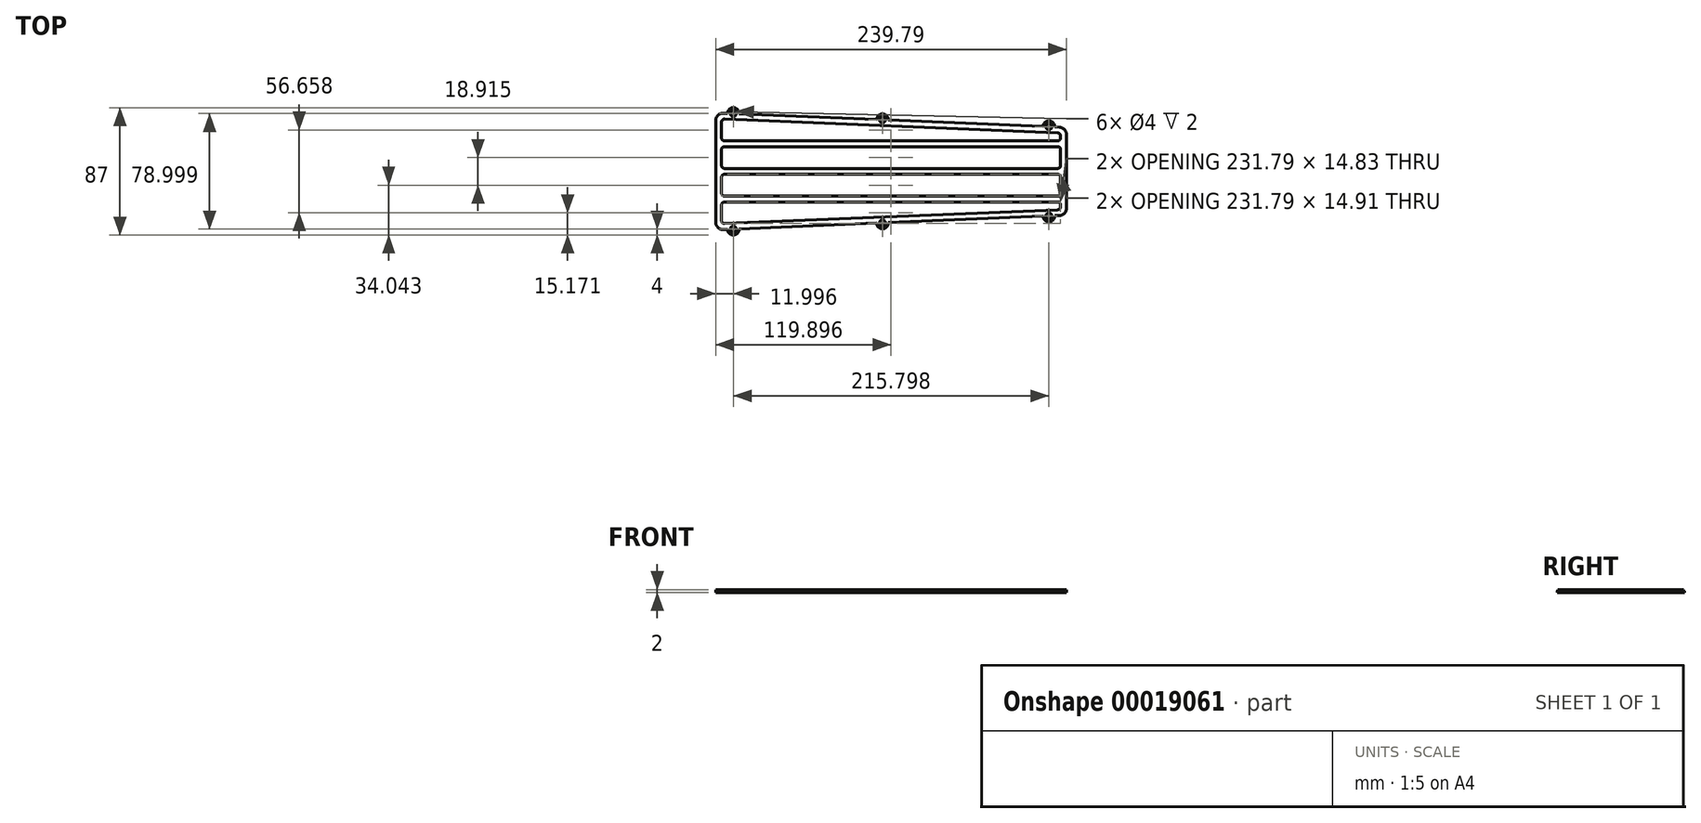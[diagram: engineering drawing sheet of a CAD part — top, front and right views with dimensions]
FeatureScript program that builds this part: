
annotation { "Feature Type Name" : "Feature", "Feature Type Description" : "" }
export const myFeature = defineFeature(function(context is Context, id is Id, definition is map)
    precondition{}
    {
        {
            var Q0;
            Q0=qCreatedBy(makeId("Top.planeOp"),FACE);
            var sketch = newSketch(context, id + "F0", { "sketchPlane" : qUnion([Q0])});
            skLineSegment(sketch, "E0.top", {"start": v(0, 80) * mm, "end": v(239.8, 70) * mm});
            skLineSegment(sketch, "E0.left", {"start": v(0, 0) * mm, "end": v(0, 80) * mm});
            skLineSegment(sketch, "E0.right", {"start": v(239.8, 10) * mm, "end": v(239.8, 70) * mm});
            skLineSegment(sketch, "E1", {"start": v(0, 0) * mm, "end": v(239.8, 10) * mm});
            skLineSegment(sketch, "E2", {"start": v(0, 40) * mm, "end": v(239.8, 40) * mm, "construction": true});
            skSolve(sketch);
        }
        {
            var Q0;
            Q0 = qSketchRegion(id + "F0", true);
            extrude(context, id + "F1", {"entities" : qUnion([Q0]), "depth" : 2 * mm});
        }
        {
            var Q0;
            Q0=makeQuery(id+"F1.opExtrude","CAP_FACE",FACE,{"disambiguationData":[OSD([sQuery(id+"F0.wireOp",EDGE,"E0.top"),sQuery(id+"F0.wireOp",EDGE,"E0.left"),sQuery(id+"F0.wireOp",EDGE,"E0.right"),sQuery(id+"F0.wireOp",EDGE,"E1")])],"isStart":false});
            var sketch = newSketch(context, id + "F2", { "sketchPlane" : qUnion([Q0])});
            skLineSegment(sketch, "E3", {"start": v(4, 75.83) * mm, "end": v(4, 60.91) * mm});
            skLineSegment(sketch, "E4", {"start": v(4, 60.91) * mm, "end": v(235.8, 60.91) * mm});
            skLineSegment(sketch, "E5", {"start": v(235.8, 60.91) * mm, "end": v(235.8, 66.16) * mm});
            skLineSegment(sketch, "E6", {"start": v(235.8, 66.16) * mm, "end": v(4, 75.83) * mm});
            skLineSegment(sketch, "E7", {"start": v(4, 19.09) * mm, "end": v(4, 4.17) * mm});
            skLineSegment(sketch, "E8", {"start": v(4, 4.17) * mm, "end": v(235.8, 13.84) * mm});
            skLineSegment(sketch, "E9", {"start": v(235.8, 13.84) * mm, "end": v(235.8, 19.09) * mm});
            skLineSegment(sketch, "E10", {"start": v(235.8, 19.09) * mm, "end": v(4, 19.09) * mm});
            skLineSegment(sketch, "E11", {"start": v(4, 23.09) * mm, "end": v(4, 38) * mm});
            skLineSegment(sketch, "E12", {"start": v(4, 23.09) * mm, "end": v(235.8, 23.09) * mm});
            skLineSegment(sketch, "E13", {"start": v(235.8, 38) * mm, "end": v(235.8, 23.09) * mm});
            skLineSegment(sketch, "E14", {"start": v(235.8, 38) * mm, "end": v(4, 38) * mm});
            skLineSegment(sketch, "E15", {"start": v(4, 42) * mm, "end": v(4, 56.91) * mm});
            skLineSegment(sketch, "E16", {"start": v(4, 42) * mm, "end": v(235.8, 42) * mm});
            skLineSegment(sketch, "E17", {"start": v(235.8, 56.91) * mm, "end": v(235.8, 42) * mm});
            skLineSegment(sketch, "E18", {"start": v(235.8, 56.91) * mm, "end": v(4, 56.91) * mm});
            skLineSegment(sketch, "E19", {"start": v(235.8, 60.91) * mm, "end": v(235.8, 56.91) * mm, "construction": true});
            skLineSegment(sketch, "E20", {"start": v(235.8, 42) * mm, "end": v(235.8, 38) * mm, "construction": true});
            skLineSegment(sketch, "E21", {"start": v(235.8, 23.09) * mm, "end": v(235.8, 19.09) * mm, "construction": true});
            skLineSegment(sketch, "E22", {"start": v(0, 40) * mm, "end": v(235.8, 40) * mm, "construction": true});
            skSolve(sketch);
        }
        {
            var Q0;
            Q0 = qSketchRegion(id + "F2", true);
            extrude(context, id + "F3", {"entities" : qUnion([Q0]), "operationType" : NewBodyOperationType.REMOVE, "oppositeDirection" : true, "depth" : 25 * mm});
        }
        {
            var Q0;
            Q0=makeQuery(id+"F3.boolean.opBoolean","COPY",EDGE,{"derivedFrom":makeQuery(id+"F3.opExtrude","SWEPT_EDGE",EDGE,{"disambiguationData":[OSD([sQuery(id+"F2.wireOp",EDGE,"E3"),sQuery(id+"F2.wireOp",EDGE,"E6")])]})});
            var Q1;
            Q1=makeQuery(id+"F3.boolean.opBoolean","COPY",EDGE,{"derivedFrom":makeQuery(id+"F3.opExtrude","SWEPT_EDGE",EDGE,{"disambiguationData":[OSD([sQuery(id+"F2.wireOp",EDGE,"E3"),sQuery(id+"F2.wireOp",EDGE,"E4")])]})});
            var Q2;
            Q2=makeQuery(id+"F3.boolean.opBoolean","COPY",EDGE,{"derivedFrom":makeQuery(id+"F3.opExtrude","SWEPT_EDGE",EDGE,{"disambiguationData":[OSD([sQuery(id+"F2.wireOp",EDGE,"E15"),sQuery(id+"F2.wireOp",EDGE,"E18")])]})});
            var Q3;
            Q3=makeQuery(id+"F3.boolean.opBoolean","COPY",EDGE,{"derivedFrom":makeQuery(id+"F3.opExtrude","SWEPT_EDGE",EDGE,{"disambiguationData":[OSD([sQuery(id+"F2.wireOp",EDGE,"E15"),sQuery(id+"F2.wireOp",EDGE,"E16")])]})});
            var Q4;
            Q4=makeQuery(id+"F3.boolean.opBoolean","COPY",EDGE,{"derivedFrom":makeQuery(id+"F3.opExtrude","SWEPT_EDGE",EDGE,{"disambiguationData":[OSD([sQuery(id+"F2.wireOp",EDGE,"E11"),sQuery(id+"F2.wireOp",EDGE,"E14")])]})});
            var Q5;
            Q5=makeQuery(id+"F3.boolean.opBoolean","COPY",EDGE,{"derivedFrom":makeQuery(id+"F3.opExtrude","SWEPT_EDGE",EDGE,{"disambiguationData":[OSD([sQuery(id+"F2.wireOp",EDGE,"E11"),sQuery(id+"F2.wireOp",EDGE,"E12")])]})});
            var Q6;
            Q6=makeQuery(id+"F3.boolean.opBoolean","COPY",EDGE,{"derivedFrom":makeQuery(id+"F3.opExtrude","SWEPT_EDGE",EDGE,{"disambiguationData":[OSD([sQuery(id+"F2.wireOp",EDGE,"E7"),sQuery(id+"F2.wireOp",EDGE,"E8")])]})});
            var Q7;
            Q7=makeQuery(id+"F3.boolean.opBoolean","COPY",EDGE,{"derivedFrom":makeQuery(id+"F3.opExtrude","SWEPT_EDGE",EDGE,{"disambiguationData":[OSD([sQuery(id+"F2.wireOp",EDGE,"E7"),sQuery(id+"F2.wireOp",EDGE,"E10")])]})});
            var Q8;
            Q8=makeQuery(id+"F3.boolean.opBoolean","COPY",EDGE,{"derivedFrom":makeQuery(id+"F3.opExtrude","SWEPT_EDGE",EDGE,{"disambiguationData":[OSD([sQuery(id+"F2.wireOp",EDGE,"E5"),sQuery(id+"F2.wireOp",EDGE,"E6")])]})});
            var Q9;
            Q9=makeQuery(id+"F3.boolean.opBoolean","COPY",EDGE,{"derivedFrom":makeQuery(id+"F3.opExtrude","SWEPT_EDGE",EDGE,{"disambiguationData":[OSD([sQuery(id+"F2.wireOp",EDGE,"E4"),sQuery(id+"F2.wireOp",EDGE,"E5")])]})});
            var Q10;
            Q10=makeQuery(id+"F3.boolean.opBoolean","COPY",EDGE,{"derivedFrom":makeQuery(id+"F3.opExtrude","SWEPT_EDGE",EDGE,{"disambiguationData":[OSD([sQuery(id+"F2.wireOp",EDGE,"E16"),sQuery(id+"F2.wireOp",EDGE,"E17")])]})});
            var Q11;
            Q11=makeQuery(id+"F3.boolean.opBoolean","COPY",EDGE,{"derivedFrom":makeQuery(id+"F3.opExtrude","SWEPT_EDGE",EDGE,{"disambiguationData":[OSD([sQuery(id+"F2.wireOp",EDGE,"E17"),sQuery(id+"F2.wireOp",EDGE,"E18")])]})});
            var Q12;
            Q12=makeQuery(id+"F3.boolean.opBoolean","COPY",EDGE,{"derivedFrom":makeQuery(id+"F3.opExtrude","SWEPT_EDGE",EDGE,{"disambiguationData":[OSD([sQuery(id+"F2.wireOp",EDGE,"E13"),sQuery(id+"F2.wireOp",EDGE,"E14")])]})});
            var Q13;
            Q13=makeQuery(id+"F3.boolean.opBoolean","COPY",EDGE,{"derivedFrom":makeQuery(id+"F3.opExtrude","SWEPT_EDGE",EDGE,{"disambiguationData":[OSD([sQuery(id+"F2.wireOp",EDGE,"E12"),sQuery(id+"F2.wireOp",EDGE,"E13")])]})});
            var Q14;
            Q14=makeQuery(id+"F3.boolean.opBoolean","COPY",EDGE,{"derivedFrom":makeQuery(id+"F3.opExtrude","SWEPT_EDGE",EDGE,{"disambiguationData":[OSD([sQuery(id+"F2.wireOp",EDGE,"E8"),sQuery(id+"F2.wireOp",EDGE,"E9")])]})});
            var Q15;
            Q15=makeQuery(id+"F3.boolean.opBoolean","COPY",EDGE,{"derivedFrom":makeQuery(id+"F3.opExtrude","SWEPT_EDGE",EDGE,{"disambiguationData":[OSD([sQuery(id+"F2.wireOp",EDGE,"E9"),sQuery(id+"F2.wireOp",EDGE,"E10")])]})});
            fillet(context, id + "F4", {"entities" : qUnion([Q0, Q1, Q2, Q3, Q4, Q5, Q6, Q7, Q8, Q9, Q10, Q11, Q12, Q13, Q14, Q15]), "radius" : 2 * mm, "tangentPropagation" : true, "allowEdgeOverflow" : false});
        }
        {
            var Q0;
            Q0=makeQuery(id+"F1.opExtrude","SWEPT_EDGE",EDGE,{"disambiguationData":[OSD([sQuery(id+"F0.wireOp",EDGE,"E0.right"),sQuery(id+"F0.wireOp",EDGE,"E1")])]});
            var Q1;
            Q1=makeQuery(id+"F1.opExtrude","SWEPT_EDGE",EDGE,{"disambiguationData":[OSD([sQuery(id+"F0.wireOp",EDGE,"E0.top"),sQuery(id+"F0.wireOp",EDGE,"E0.right")])]});
            var Q2;
            Q2=makeQuery(id+"F1.opExtrude","SWEPT_EDGE",EDGE,{"disambiguationData":[OSD([sQuery(id+"F0.wireOp",EDGE,"E0.left"),sQuery(id+"F0.wireOp",EDGE,"E1")])]});
            var Q3;
            Q3=makeQuery(id+"F1.opExtrude","SWEPT_EDGE",EDGE,{"disambiguationData":[OSD([sQuery(id+"F0.wireOp",EDGE,"E0.top"),sQuery(id+"F0.wireOp",EDGE,"E0.left")])]});
            fillet(context, id + "F5", {"entities" : qUnion([Q0, Q1, Q2, Q3]), "radius" : 5 * mm, "tangentPropagation" : true, "allowEdgeOverflow" : false});
        }
        {
            var Q0;
            Q0=makeQuery(id+"F1.opExtrude","CAP_FACE",FACE,{"disambiguationData":[OSD([sQuery(id+"F0.wireOp",EDGE,"E0.top"),sQuery(id+"F0.wireOp",EDGE,"E0.left"),sQuery(id+"F0.wireOp",EDGE,"E0.right"),sQuery(id+"F0.wireOp",EDGE,"E1")])],"isStart":false});
            var sketch = newSketch(context, id + "F6", { "sketchPlane" : qUnion([Q0])});
            skArc(sketch, "E23", {"start": v(16, 79.33) * mm, "mid": v(12.16, 83.5) * mm, "end": v(8, 79.67) * mm});
            skLineSegment(sketch, "E24", {"start": v(8, 79.67) * mm, "end": v(16, 79.33) * mm});
            skLineSegment(sketch, "E25", {"start": v(8, 79.67) * mm, "end": v(8, 0.33) * mm, "construction": true});
            skArc(sketch, "E26", {"start": v(8, 0.33) * mm, "mid": v(12.16, -3.5) * mm, "end": v(16, 0.67) * mm});
            skLineSegment(sketch, "E27", {"start": v(8, 0.33) * mm, "end": v(16, 0.67) * mm});
            skLineSegment(sketch, "E28", {"start": v(231.8, 70.33) * mm, "end": v(231.8, 9.67) * mm, "construction": true});
            skArc(sketch, "E29", {"start": v(231.8, 70.33) * mm, "mid": v(227.96, 74.5) * mm, "end": v(223.8, 70.67) * mm});
            skArc(sketch, "E30", {"start": v(223.8, 9.33) * mm, "mid": v(227.96, 5.5) * mm, "end": v(231.8, 9.67) * mm});
            skLineSegment(sketch, "E31", {"start": v(223.8, 70.67) * mm, "end": v(231.8, 70.33) * mm});
            skLineSegment(sketch, "E32", {"start": v(231.8, 9.67) * mm, "end": v(223.8, 9.33) * mm});
            skLineSegment(sketch, "E33", {"start": v(110, 75.41) * mm, "end": v(110, 4.59) * mm, "construction": true});
            skArc(sketch, "E34", {"start": v(118, 75.08) * mm, "mid": v(114.16, 79.24) * mm, "end": v(110, 75.41) * mm});
            skArc(sketch, "E35", {"start": v(110, 4.59) * mm, "mid": v(114.16, 0.76) * mm, "end": v(118, 4.92) * mm});
            skLineSegment(sketch, "E36", {"start": v(110, 75.41) * mm, "end": v(118, 75.08) * mm});
            skLineSegment(sketch, "E37", {"start": v(110, 4.59) * mm, "end": v(118, 4.92) * mm});
            skSolve(sketch);
        }
        {
            var Q0;
            Q0 = qSketchRegion(id + "F6", true);
            var Q1;
            Q1=makeQuery(id+"F1.opExtrude","CAP_FACE",FACE,{"disambiguationData":[OSD([sQuery(id+"F0.wireOp",EDGE,"E0.top"),sQuery(id+"F0.wireOp",EDGE,"E0.left"),sQuery(id+"F0.wireOp",EDGE,"E0.right"),sQuery(id+"F0.wireOp",EDGE,"E1")])],"isStart":true});
            extrude(context, id + "F7", {"entities" : qUnion([Q0]), "operationType" : NewBodyOperationType.ADD, "endBound" : BoundingType.UP_TO_SURFACE, "oppositeDirection" : true, "endBoundEntityFace" : qUnion([Q1]), "depth" : 25 * mm});
        }
        {
            var Q0;
            Q0=makeQuery(id+"F7.boolean.opBoolean","MERGE",FACE,{"derivedFrom":[makeQuery(id+"F1.opExtrude","CAP_FACE",FACE,{"disambiguationData":[OSD([sQuery(id+"F0.wireOp",EDGE,"E0.top"),sQuery(id+"F0.wireOp",EDGE,"E0.left"),sQuery(id+"F0.wireOp",EDGE,"E0.right"),sQuery(id+"F0.wireOp",EDGE,"E1")])],"isStart":false}),makeQuery(id+"F7.opExtrude","CAP_FACE",FACE,{"disambiguationData":[OSD([sQuery(id+"F6.wireOp",EDGE,"E23"),sQuery(id+"F6.wireOp",EDGE,"E24")])],"isStart":true}),makeQuery(id+"F7.opExtrude","CAP_FACE",FACE,{"disambiguationData":[OSD([sQuery(id+"F6.wireOp",EDGE,"E26"),sQuery(id+"F6.wireOp",EDGE,"E27")])],"isStart":true}),makeQuery(id+"F7.opExtrude","CAP_FACE",FACE,{"disambiguationData":[OSD([sQuery(id+"F6.wireOp",EDGE,"E29"),sQuery(id+"F6.wireOp",EDGE,"E31")])],"isStart":true}),makeQuery(id+"F7.opExtrude","CAP_FACE",FACE,{"disambiguationData":[OSD([sQuery(id+"F6.wireOp",EDGE,"E30"),sQuery(id+"F6.wireOp",EDGE,"E32")])],"isStart":true}),makeQuery(id+"F7.opExtrude","CAP_FACE",FACE,{"disambiguationData":[OSD([sQuery(id+"F6.wireOp",EDGE,"E34"),sQuery(id+"F6.wireOp",EDGE,"E36")])],"isStart":true}),makeQuery(id+"F7.opExtrude","CAP_FACE",FACE,{"disambiguationData":[OSD([sQuery(id+"F6.wireOp",EDGE,"E35"),sQuery(id+"F6.wireOp",EDGE,"E37")])],"isStart":true})]});
            var sketch = newSketch(context, id + "F8", { "sketchPlane" : qUnion([Q0])});
            skCircle(sketch, "E38", {"center": v(12, 79.5) * mm, "radius": 2 * mm});
            skCircle(sketch, "E39", {"center": v(114, 75.25) * mm, "radius": 2 * mm});
            skCircle(sketch, "E40", {"center": v(227.8, 70.5) * mm, "radius": 2 * mm});
            skCircle(sketch, "E41", {"center": v(227.8, 9.5) * mm, "radius": 2 * mm});
            skCircle(sketch, "E42", {"center": v(114, 4.75) * mm, "radius": 2 * mm});
            skCircle(sketch, "E43", {"center": v(12, 0.5) * mm, "radius": 2 * mm});
            skSolve(sketch);
        }
        {
            var Q0;
            Q0 = qSketchRegion(id + "F8", true);
            extrude(context, id + "F9", {"entities" : qUnion([Q0]), "operationType" : NewBodyOperationType.REMOVE, "oppositeDirection" : true, "depth" : 25 * mm});
        }
        {
            var Q0;
            Q0=makeQuery(id+"F7.boolean.opBoolean","MERGE",FACE,{"derivedFrom":[makeQuery(id+"F1.opExtrude","CAP_FACE",FACE,{"disambiguationData":[OSD([sQuery(id+"F0.wireOp",EDGE,"E0.top"),sQuery(id+"F0.wireOp",EDGE,"E0.left"),sQuery(id+"F0.wireOp",EDGE,"E0.right"),sQuery(id+"F0.wireOp",EDGE,"E1")])],"isStart":false}),makeQuery(id+"F7.opExtrude","CAP_FACE",FACE,{"disambiguationData":[OSD([sQuery(id+"F6.wireOp",EDGE,"E23"),sQuery(id+"F6.wireOp",EDGE,"E24")])],"isStart":true}),makeQuery(id+"F7.opExtrude","CAP_FACE",FACE,{"disambiguationData":[OSD([sQuery(id+"F6.wireOp",EDGE,"E26"),sQuery(id+"F6.wireOp",EDGE,"E27")])],"isStart":true}),makeQuery(id+"F7.opExtrude","CAP_FACE",FACE,{"disambiguationData":[OSD([sQuery(id+"F6.wireOp",EDGE,"E29"),sQuery(id+"F6.wireOp",EDGE,"E31")])],"isStart":true}),makeQuery(id+"F7.opExtrude","CAP_FACE",FACE,{"disambiguationData":[OSD([sQuery(id+"F6.wireOp",EDGE,"E30"),sQuery(id+"F6.wireOp",EDGE,"E32")])],"isStart":true}),makeQuery(id+"F7.opExtrude","CAP_FACE",FACE,{"disambiguationData":[OSD([sQuery(id+"F6.wireOp",EDGE,"E34"),sQuery(id+"F6.wireOp",EDGE,"E36")])],"isStart":true}),makeQuery(id+"F7.opExtrude","CAP_FACE",FACE,{"disambiguationData":[OSD([sQuery(id+"F6.wireOp",EDGE,"E35"),sQuery(id+"F6.wireOp",EDGE,"E37")])],"isStart":true})]});
            var sketch = newSketch(context, id + "F10", { "sketchPlane" : qUnion([Q0])});
            skLineSegment(sketch, "E44.bottom", {"start": v(10, 83.5) * mm, "end": v(14, 83.5) * mm});
            skLineSegment(sketch, "E44.top", {"start": v(10, 79.5) * mm, "end": v(14, 79.5) * mm});
            skLineSegment(sketch, "E44.left", {"start": v(10, 83.5) * mm, "end": v(10, 79.5) * mm});
            skLineSegment(sketch, "E44.right", {"start": v(14, 83.5) * mm, "end": v(14, 79.5) * mm});
            skLineSegment(sketch, "E45.bottom", {"start": v(112, 79.25) * mm, "end": v(116, 79.25) * mm});
            skLineSegment(sketch, "E45.top", {"start": v(112, 75.25) * mm, "end": v(116, 75.25) * mm});
            skLineSegment(sketch, "E45.left", {"start": v(112, 79.25) * mm, "end": v(112, 75.25) * mm});
            skLineSegment(sketch, "E45.right", {"start": v(116, 79.25) * mm, "end": v(116, 75.25) * mm});
            skLineSegment(sketch, "E46.bottom", {"start": v(225.8, 74.5) * mm, "end": v(229.8, 74.5) * mm});
            skLineSegment(sketch, "E46.top", {"start": v(225.8, 70.5) * mm, "end": v(229.8, 70.5) * mm});
            skLineSegment(sketch, "E46.left", {"start": v(225.8, 74.5) * mm, "end": v(225.8, 70.5) * mm});
            skLineSegment(sketch, "E46.right", {"start": v(229.8, 74.5) * mm, "end": v(229.8, 70.5) * mm});
            skLineSegment(sketch, "E47.bottom", {"start": v(10, 0.5) * mm, "end": v(14, 0.5) * mm});
            skLineSegment(sketch, "E47.top", {"start": v(10, -3.5) * mm, "end": v(14, -3.5) * mm});
            skLineSegment(sketch, "E47.left", {"start": v(10, 0.5) * mm, "end": v(10, -3.5) * mm});
            skLineSegment(sketch, "E47.right", {"start": v(14, 0.5) * mm, "end": v(14, -3.5) * mm});
            skLineSegment(sketch, "E48.bottom", {"start": v(112, 4.75) * mm, "end": v(116, 4.75) * mm});
            skLineSegment(sketch, "E48.top", {"start": v(112, 0.75) * mm, "end": v(116, 0.75) * mm});
            skLineSegment(sketch, "E48.left", {"start": v(112, 4.75) * mm, "end": v(112, 0.75) * mm});
            skLineSegment(sketch, "E48.right", {"start": v(116, 4.75) * mm, "end": v(116, 0.75) * mm});
            skLineSegment(sketch, "E49.bottom", {"start": v(225.8, 9.5) * mm, "end": v(229.8, 9.5) * mm});
            skLineSegment(sketch, "E49.top", {"start": v(225.8, 5.5) * mm, "end": v(229.8, 5.5) * mm});
            skLineSegment(sketch, "E49.left", {"start": v(225.8, 9.5) * mm, "end": v(225.8, 5.5) * mm});
            skLineSegment(sketch, "E49.right", {"start": v(229.8, 9.5) * mm, "end": v(229.8, 5.5) * mm});
            skSolve(sketch);
        }
        {
            var Q0;
            Q0 = qSketchRegion(id + "F10", true);
            extrude(context, id + "F11", {"entities" : qUnion([Q0]), "operationType" : NewBodyOperationType.REMOVE, "oppositeDirection" : true, "depth" : 1 * mm});
        }
    });
